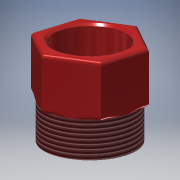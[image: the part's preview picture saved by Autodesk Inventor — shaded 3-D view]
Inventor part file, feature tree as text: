
AUTODESK INVENTOR PART (.ipt)
format: ipt  version: 2018 (Build 220112000, 112)  size: 223,232 bytes
history: native  units: mm
features: extrude x3, sketch x3, fillet x2, chamfer x1, thread x1
ambient origin geometry x8: Origin, YZ Plane, XZ Plane, XY Plane, X Axis, Y Axis, Z Axis, Center Point
bodies: Solid1 (feature_tree)
feature tree (10):
  extrude  "Extrusion1"  Depth=10.0mm TaperAngle=0.0deg
  extrude  "Extrusion2"  Depth=10.0mm
  extrude  "Extrusion3"  Depth=0.5mm TaperAngle=45.0deg
  chamfer  "Chamfer1"  Distance=0.5mm
  fillet  "Fillet1"  Radius=0.5mm
  fillet  "Fillet2"  Radius=4.0mm
  thread  "Thread1"  [1 undecoded]
  sketch  "Sketch1"  dims[d0=10.0mm d1=6.0mm d2=0.0mm]
  sketch  "Sketch2"  dims[d3=10.0mm d4=0.0mm d5=8.0mm]
  sketch  "Sketch3"  dims[d6=6.0mm d7=0.0mm d8=0.25mm d9=2.0mm d10=45.0deg d11=0.5mm d12=0.5mm d13=4.0mm d14=0.0mm]
note: 1 required parameter value undecoded (feature->parameter linkage not recoverable at this tier; creation-order binding heuristic only, values carry confidence <= 0.55)
